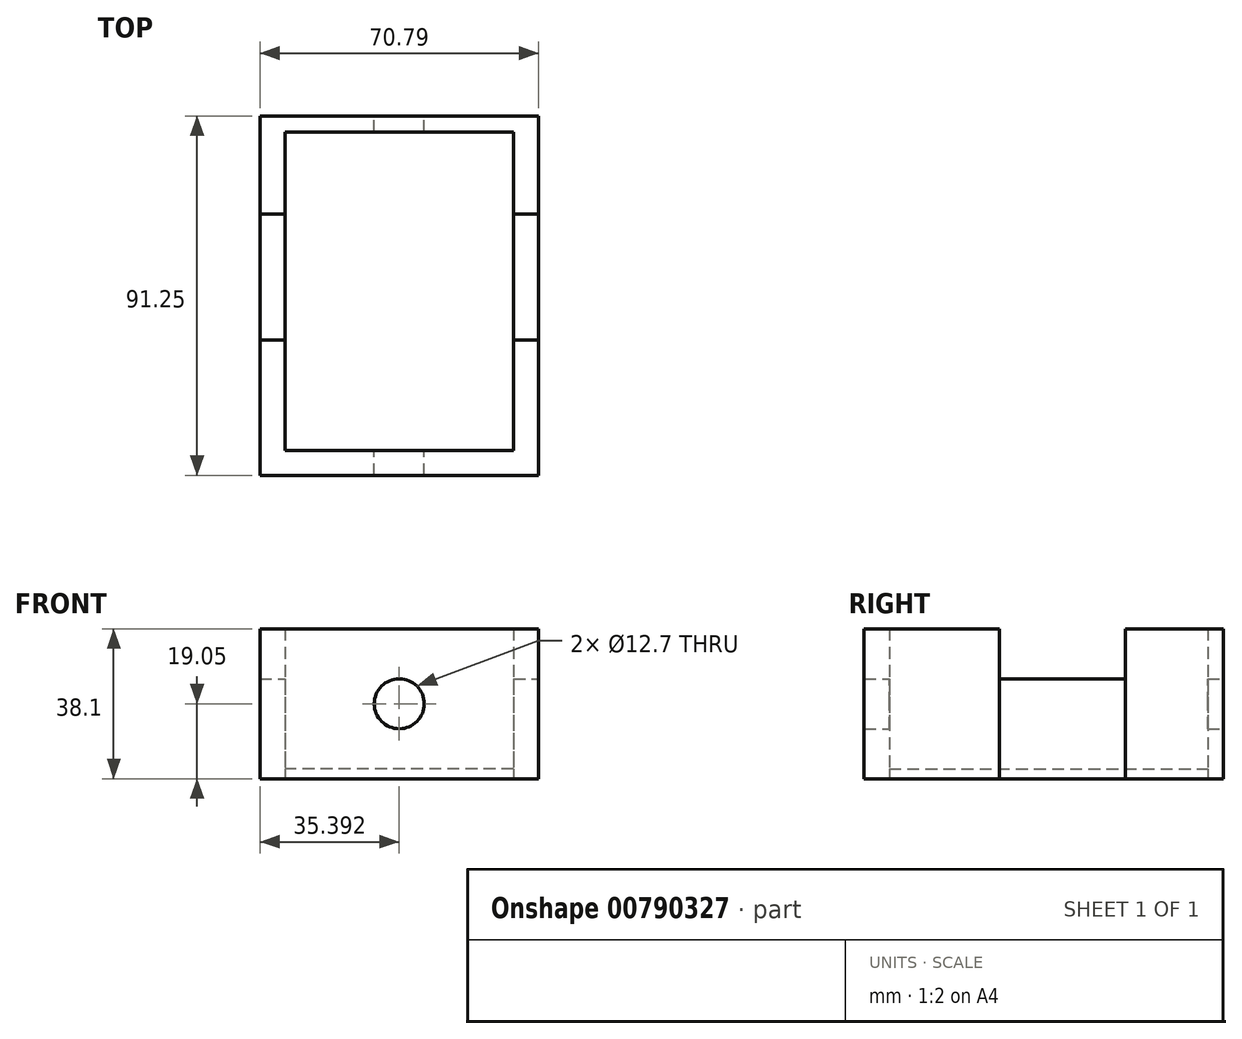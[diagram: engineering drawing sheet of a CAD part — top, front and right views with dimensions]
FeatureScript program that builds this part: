
annotation { "Feature Type Name" : "Feature", "Feature Type Description" : "" }
export const myFeature = defineFeature(function(context is Context, id is Id, definition is map)
    precondition{}
    {
        {
            var Q0;
            Q0=qCreatedBy(makeId("Top.planeOp"),FACE);
            var sketch = newSketch(context, id + "F0", { "sketchPlane" : qUnion([Q0])});
            skLineSegment(sketch, "E0", {"start": v(-43.85, 47.43) * mm, "end": v(-43.85, -43.82) * mm});
            skLineSegment(sketch, "E1", {"start": v(-43.85, -43.82) * mm, "end": v(26.94, -43.82) * mm});
            skLineSegment(sketch, "E2", {"start": v(26.94, -43.82) * mm, "end": v(26.94, 47.43) * mm});
            skLineSegment(sketch, "E3", {"start": v(26.94, 47.43) * mm, "end": v(-43.85, 47.43) * mm});
            skLineSegment(sketch, "E4", {"start": v(-37.5, 43.44) * mm, "end": v(-37.5, -37.47) * mm});
            skLineSegment(sketch, "E5", {"start": v(-37.5, -37.47) * mm, "end": v(20.59, -37.47) * mm});
            skLineSegment(sketch, "E6", {"start": v(20.59, -37.47) * mm, "end": v(20.59, 43.44) * mm});
            skLineSegment(sketch, "E7", {"start": v(20.59, 43.44) * mm, "end": v(-37.5, 43.44) * mm});
            skLineSegment(sketch, "E8", {"start": v(-43.85, -9.48) * mm, "end": v(-37.5, -9.48) * mm});
            skLineSegment(sketch, "E9", {"start": v(-43.85, 22.5) * mm, "end": v(-37.5, 22.5) * mm});
            skLineSegment(sketch, "E10", {"start": v(20.59, 22.5) * mm, "end": v(26.94, 22.5) * mm});
            skLineSegment(sketch, "E11", {"start": v(20.59, -9.48) * mm, "end": v(26.94, -9.48) * mm});
            skSolve(sketch);
        }
        {
            var Q0;
            {var subQ4=sQuery(id+"F0.wireOp",EDGE,"E1");Q0=makeQuery(id+"F0.imprint","IMPRINT",FACE,{"disambiguationData":[TD([[makeQuery(id+"F0.imprint","IMPRINT",EDGE,{"derivedFrom":subQ4}),1.0]])]});}
            var Q1;
            {var subQ3=sQuery(id+"F0.wireOp",EDGE,"E3");Q1=makeQuery(id+"F0.imprint","IMPRINT",FACE,{"disambiguationData":[TD([[makeQuery(id+"F0.imprint","IMPRINT",EDGE,{"derivedFrom":subQ3}),1.0]])]});}
            extrude(context, id + "F1", {"entities" : qUnion([Q0, Q1]), "depth" : 38.1 * mm, "offsetDistance" : 25.4 * mm});
        }
        {
            var Q0;
            {var subQ0=sQuery(id+"F0.wireOp",EDGE,"E8");Q0=makeQuery(id+"F0.imprint","IMPRINT",FACE,{"disambiguationData":[TD([[makeQuery(id+"F0.imprint","IMPRINT",EDGE,{"derivedFrom":subQ0}),1.0]])]});}
            var Q1;
            {var subQ0=sQuery(id+"F0.wireOp",EDGE,"E10");Q1=makeQuery(id+"F0.imprint","IMPRINT",FACE,{"disambiguationData":[TD([[makeQuery(id+"F0.imprint","IMPRINT",EDGE,{"derivedFrom":subQ0}),-1.0]])]});}
            extrude(context, id + "F2", {"entities" : qUnion([Q0, Q1]), "depth" : 25.4 * mm, "offsetDistance" : 25.4 * mm});
        }
        {
            var Q0;
            {var subQ0=sQuery(id+"F0.wireOp",EDGE,"E5");Q0=makeQuery(id+"F0.imprint","IMPRINT",FACE,{"disambiguationData":[TD([[makeQuery(id+"F0.imprint","IMPRINT",EDGE,{"derivedFrom":subQ0}),1.0]])]});}
            extrude(context, id + "F3", {"entities" : qUnion([Q0]), "depth" : 2.54 * mm, "offsetDistance" : 25.4 * mm});
        }
        {
            var Q0;
            Q0=makeQuery(id+"F1.opExtrude","SWEPT_FACE",FACE,{"disambiguationData":[OSD([sQuery(id+"F0.wireOp",EDGE,"E3")])]});
            var sketch = newSketch(context, id + "F4", { "sketchPlane" : qUnion([Q0])});
            skLineSegment(sketch, "E12", {"start": v(-26.94, 19.05) * mm, "end": v(43.85, 19.05) * mm});
            skLineSegment(sketch, "E13", {"start": v(8.46, 38.1) * mm, "end": v(8.46, 0) * mm});
            skPoint(sketch, "E14", {"position": v(8.46, 19.05) * mm});
            skSolve(sketch);
        }
        {
            var Q0;
            Q0=sQuery(id+"F4.wireOp",VERTEX,"E14");
            var Q1;
            Q1=makeQuery(id+"F1.opExtrude","SWEPT_BODY",BODY,{"disambiguationData":[OSD([sQuery(id+"F0.wireOp",EDGE,"E0"),sQuery(id+"F0.wireOp",EDGE,"E2"),sQuery(id+"F0.wireOp",EDGE,"E3"),sQuery(id+"F0.wireOp",EDGE,"E4"),sQuery(id+"F0.wireOp",EDGE,"E6"),sQuery(id+"F0.wireOp",EDGE,"E7"),sQuery(id+"F0.wireOp",EDGE,"E9"),sQuery(id+"F0.wireOp",EDGE,"E10")])]});
            var Q2;
            Q2=makeQuery(id+"F1.opExtrude","SWEPT_BODY",BODY,{"disambiguationData":[OSD([sQuery(id+"F0.wireOp",EDGE,"E0"),sQuery(id+"F0.wireOp",EDGE,"E1"),sQuery(id+"F0.wireOp",EDGE,"E2"),sQuery(id+"F0.wireOp",EDGE,"E4"),sQuery(id+"F0.wireOp",EDGE,"E5"),sQuery(id+"F0.wireOp",EDGE,"E6"),sQuery(id+"F0.wireOp",EDGE,"E8"),sQuery(id+"F0.wireOp",EDGE,"E11")])]});
            hole(context, id + "F5", {"style" : HoleStyle.SIMPLE, "endStyle" : HoleEndStyle.THROUGH, "holeDiameter" : 12.7 * mm, "majorDiameter" : 6.35 * mm, "isTappedThrough" : true, "tappedDepth" : 12.7 * mm, "tapClearance" : 3, "locations" : qUnion([Q0]), "scope" : qUnion([Q1, Q2])});
        }
    });
